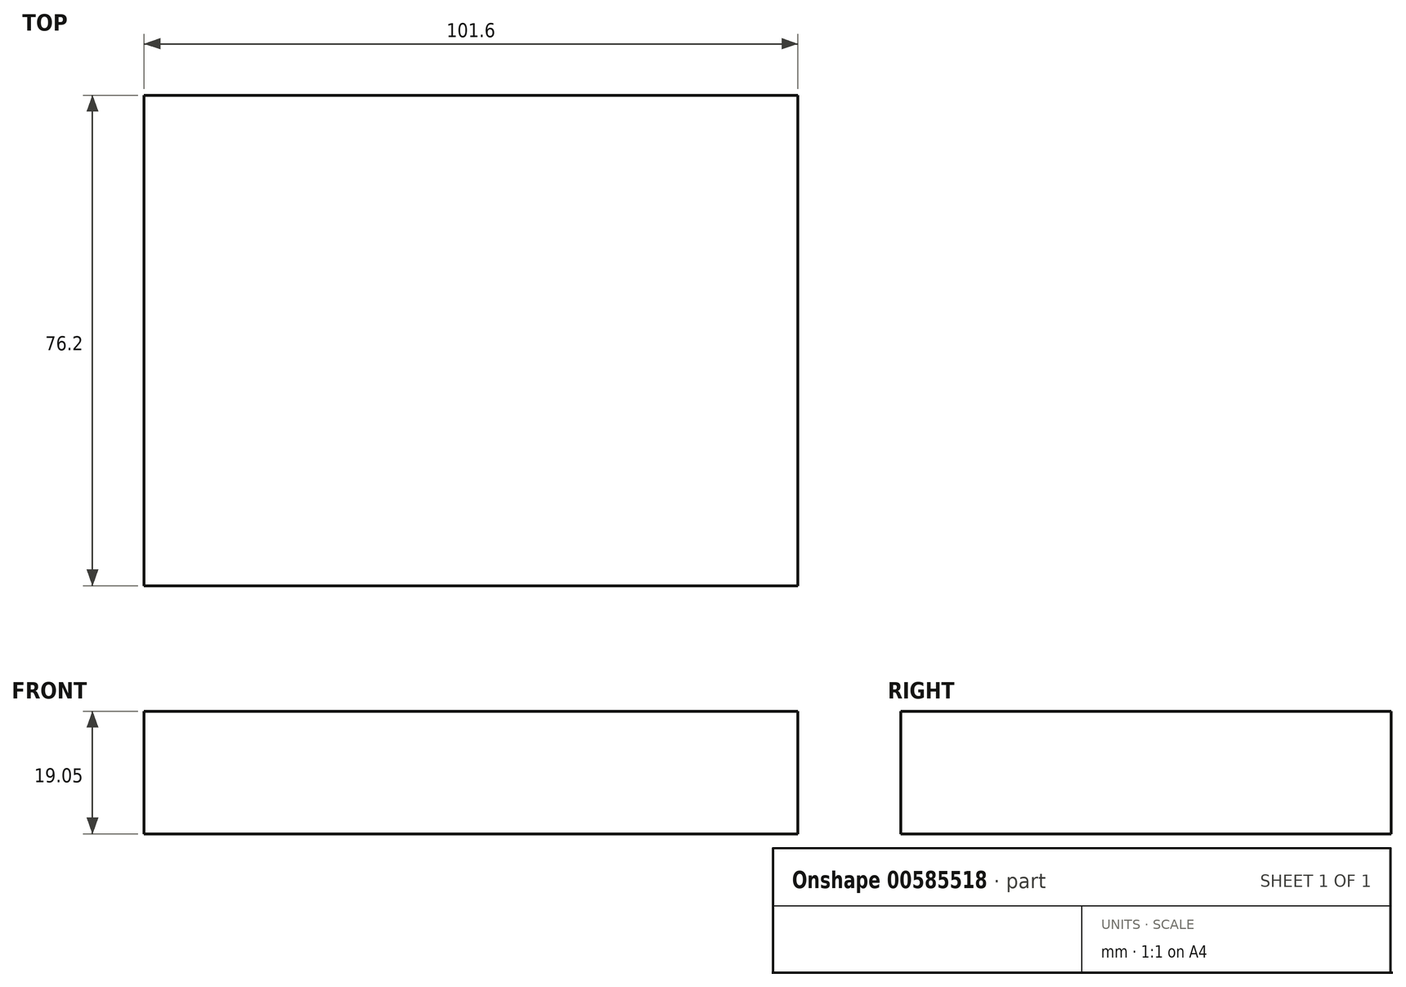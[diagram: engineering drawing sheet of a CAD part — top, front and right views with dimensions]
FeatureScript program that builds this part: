
annotation { "Feature Type Name" : "Feature", "Feature Type Description" : "" }
export const myFeature = defineFeature(function(context is Context, id is Id, definition is map)
    precondition{}
    {
        {
            var Q0;
            Q0=qCreatedBy(makeId("Top.planeOp"),FACE);
            var sketch = newSketch(context, id + "F0", { "sketchPlane" : qUnion([Q0])});
            skLineSegment(sketch, "E0.bottom", {"start": v(50.8, -38.1) * mm, "end": v(-50.8, -38.1) * mm});
            skLineSegment(sketch, "E0.top", {"start": v(50.8, 38.1) * mm, "end": v(-50.8, 38.1) * mm});
            skLineSegment(sketch, "E0.left", {"start": v(50.8, -38.1) * mm, "end": v(50.8, 38.1) * mm});
            skLineSegment(sketch, "E0.right", {"start": v(-50.8, -38.1) * mm, "end": v(-50.8, 38.1) * mm});
            skPoint(sketch, "E0.middle", {"position": v(0, 0) * mm});
            skSolve(sketch);
        }
        {
            var Q0;
            Q0=makeQuery(id+"F0.imprint","IMPRINT",FACE,{"disambiguationData":[TD([[makeQuery(id+"F0.imprint","IMPRINT",EDGE,{"derivedFrom":sQuery(id+"F0.wireOp",EDGE,"E0.bottom")}),-1.0]])]});
            extrude(context, id + "F1", {"entities" : qUnion([Q0]), "depth" : 19.05 * mm, "offsetDistance" : 25.4 * mm});
        }
    });
